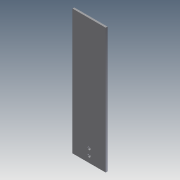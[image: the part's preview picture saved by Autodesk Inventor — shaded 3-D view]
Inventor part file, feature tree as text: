
AUTODESK INVENTOR PART (.ipt)
format: ipt  version: 2011 (Build 150239000, 239)  size: 142,336 bytes
history: native  units: in
note: dims shown in document units (in); Inventor stores cm internally (conversion verified against a paired STEP export)
features: extrude x10, sketch x10
ambient origin geometry x8: Origin, YZ Plane, XZ Plane, XY Plane, X Axis, Y Axis, Z Axis, Center Point
bodies: Solid1 (feature_tree)
feature tree (20):
  extrude  "Extrusion1"  Depth=12.0in
  extrude  "Extrusion2"  Depth=0.5in TaperAngle=0.0deg
  extrude  "Extrusion3"  Depth=10.0in
  extrude  "Extrusion4"  Depth=5.0in TaperAngle=0.0deg
  extrude  "Extrusion5"  Depth=1.0in TaperAngle=0.0deg
  extrude  "Extrusion6"  Depth=0.25in TaperAngle=0.0deg
  extrude  "Extrusion7"  Depth=0.315in
  extrude  "Extrusion8"  Depth=1.1811in
  extrude  "Extrusion9"  Depth=1.0in TaperAngle=0.0deg
  extrude  "Extrusion10"  Depth=0.5in TaperAngle=0.0deg
  sketch  "Sketch1"  dims[d0=5.5in d1=12.0in]
  sketch  "Sketch2"  dims[d2=0.25in d3=0.0in d4=0.5in d5=0.0in]
  sketch  "Sketch3"  dims[d6=1.5in d7=0.0in d9=10.0in]
  sketch  "Sketch5"  dims[d10=0.25in d11=0.0in d12=5.0in d13=0.0in]
  sketch  "Sketch6"  dims[d14=0.25in d15=1.0in d16=0.0in]
  sketch  "Sketch7"  dims[d17=0.25in d18=0.25in d19=0.0in]
  sketch  "Sketch8"  dims[d20=0.525in d21=0.315in]
  sketch  "Sketch9"  dims[d22=0.3937in d23=1.1811in]
  sketch  "Sketch10"  dims[d24=0.3937in d25=1.0in d26=0.0in]
  sketch  "Sketch11"  dims[d27=0.5in d28=0.0in d29=0.5in d30=0.0in]
